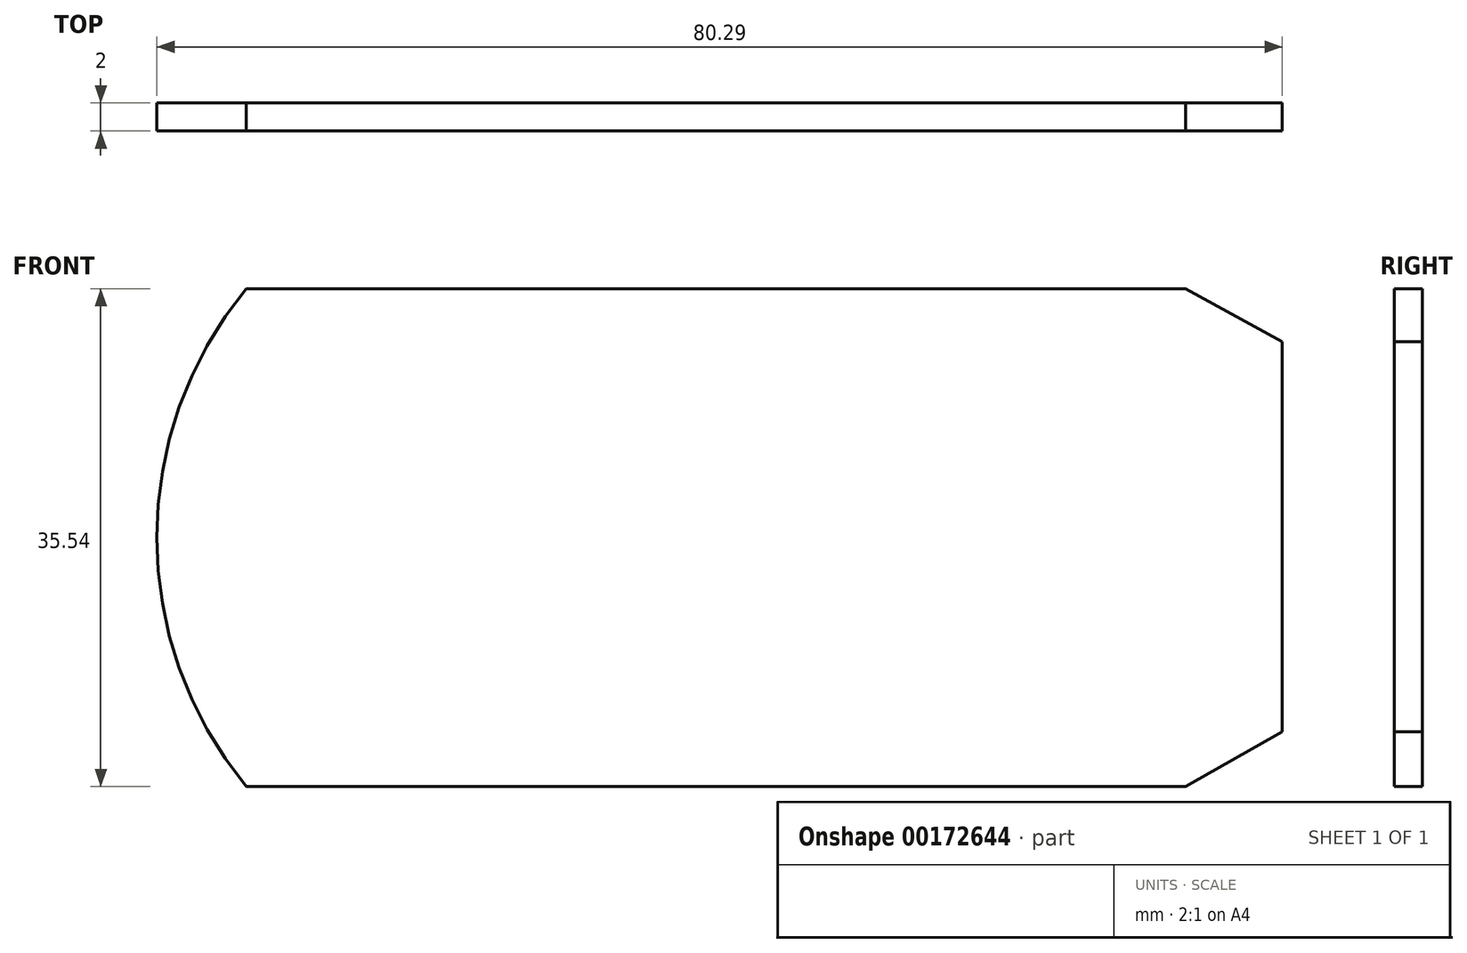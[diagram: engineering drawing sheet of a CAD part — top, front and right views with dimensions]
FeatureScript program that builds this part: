
annotation { "Feature Type Name" : "Feature", "Feature Type Description" : "" }
export const myFeature = defineFeature(function(context is Context, id is Id, definition is map)
    precondition{}
    {
        {
            var Q0;
            Q0=qCreatedBy(makeId("Front.planeOp"),FACE);
            var sketch = newSketch(context, id + "F0", { "sketchPlane" : qUnion([Q0])});
            skLineSegment(sketch, "E0.bottom", {"start": v(-33.51, -17.77) * mm, "end": v(33.51, -17.77) * mm});
            skLineSegment(sketch, "E0.top", {"start": v(-33.51, 17.77) * mm, "end": v(33.51, 17.77) * mm});
            skLineSegment(sketch, "E0.left", {"start": v(-33.51, -17.77) * mm, "end": v(-33.51, 17.77) * mm});
            skLineSegment(sketch, "E0.right", {"start": v(33.51, -17.77) * mm, "end": v(33.51, 17.77) * mm});
            skPoint(sketch, "E0.middle", {"position": v(0, 0) * mm});
            skPoint(sketch, "E1.endSnap0", {"position": v(-33.51, 0) * mm});
            skArc(sketch, "E2", {"start": v(-33.51, 17.77) * mm, "mid": v(-39.87, 0) * mm, "end": v(-33.51, -17.77) * mm});
            skLineSegment(sketch, "E3", {"start": v(33.51, 17.77) * mm, "end": v(40.42, 13.96) * mm});
            skLineSegment(sketch, "E4", {"start": v(40.42, 13.96) * mm, "end": v(40.42, -13.87) * mm});
            skLineSegment(sketch, "E5", {"start": v(40.42, -13.87) * mm, "end": v(33.51, -17.77) * mm});
            skSolve(sketch);
        }
        {
            var Q0;
            Q0 = qSketchRegion(id + "F0", true);
            extrude(context, id + "F1", {"entities" : qUnion([Q0]), "depth" : 2 * mm});
        }
    });
